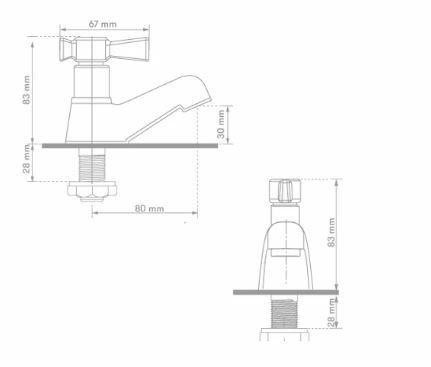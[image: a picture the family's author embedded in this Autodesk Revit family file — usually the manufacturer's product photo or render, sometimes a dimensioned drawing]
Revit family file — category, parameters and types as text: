
# Revit family: 01-1700-11 LLAVE INDIVIDUAL LAVAMANOS HELIX PALA
name_source: partatom
category: Plumbing Fixtures
revit_build: Autodesk Revit 2018 (Build: 20170223_1515(x64)
units: mm (PartAtom-declared; Revit-internal decimal feet)

## family parameters
Cut with Voids When Loaded = No
Host = Face
OmniClass Number = 23.31.11.00
Part Type = Normal
Room Calculation Point = No
Round Connector Dimension = Use Diameter
Shared = No

## types (1)
- 01-1700-11
    Alto = 83 mm  [stored 0.27231 ft]
    Base = 81 mm  [stored 0.265748 ft]
    CW Connection = Yes
    Default Elevation = 0 mm  [stored 0 ft]
    Description = Llave individual
    HW Connection = Yes
    Link Ficha Tecnica = http://infotecnica.gricol.com
    Manija = 67 mm
    Manufacturer = Gricol
    Model = 01-1700-11
    Plastico ABS Cromado = Plastico - ABS Cromado
    Product Name = LLAVE INDIVIDUAL LAVAMANOS HELIX PALA
    Type Image = LLAVE INDIVIDUAL LAVAMANOS HELIX PALA.JPG
    URL = https://www.gricol.com
    Vent Connection = No
    Waste Connection = No

note: [stored X ft] marks values corroborated as IEEE doubles in the binary element streams (Revit-internal decimal feet)

## geometry (parser evidence)
native form markers: Blend x2, Sweep x4
no freeform markers — native parametric forms only
